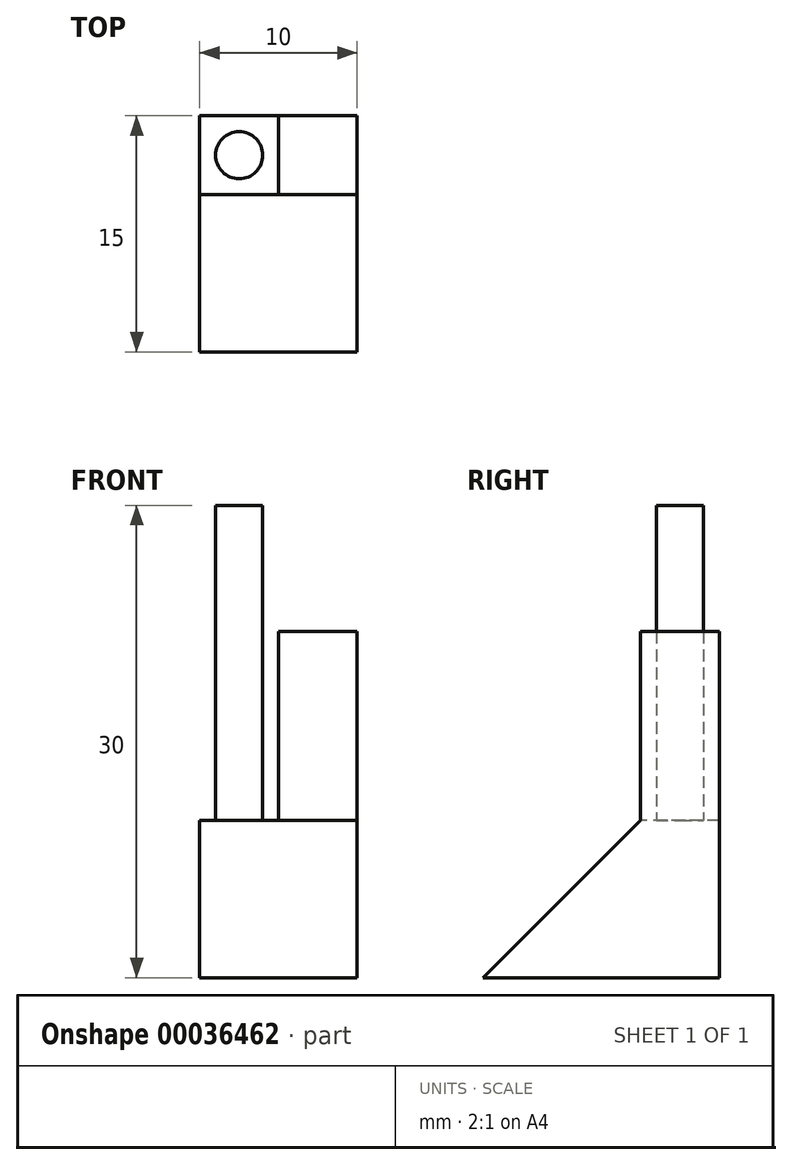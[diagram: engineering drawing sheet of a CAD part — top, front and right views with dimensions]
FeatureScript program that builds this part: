
annotation { "Feature Type Name" : "Feature", "Feature Type Description" : "" }
export const myFeature = defineFeature(function(context is Context, id is Id, definition is map)
    precondition{}
    {
        {
            var Q0;
            Q0=qCreatedBy(makeId("Right.planeOp"),FACE);
            var sketch = newSketch(context, id + "F0", { "sketchPlane" : qUnion([Q0])});
            skLineSegment(sketch, "E0", {"start": v(-10.68, 3.2) * mm, "end": v(-5.68, 3.2) * mm});
            skLineSegment(sketch, "E1", {"start": v(-5.68, 3.2) * mm, "end": v(-5.68, -6.8) * mm});
            skLineSegment(sketch, "E2", {"start": v(-5.68, -6.8) * mm, "end": v(-20.68, -6.8) * mm});
            skLineSegment(sketch, "E3", {"start": v(-20.68, -6.8) * mm, "end": v(-10.68, 3.2) * mm});
            skSolve(sketch);
        }
        {
            var Q0;
            Q0 = qSketchRegion(id + "F0", true);
            extrude(context, id + "F1", {"entities" : qUnion([Q0]), "endBound" : BoundingType.SYMMETRIC, "depth" : 10 * mm});
        }
        {
            var Q0;
            Q0=makeQuery(id+"F1.opExtrude","SWEPT_FACE",FACE,{"disambiguationData":[OSD([sQuery(id+"F0.wireOp",EDGE,"E0")])]});
            var sketch = newSketch(context, id + "F2", { "sketchPlane" : qUnion([Q0])});
            skLineSegment(sketch, "E4.bottom", {"start": v(0, -5.68) * mm, "end": v(5, -5.68) * mm});
            skLineSegment(sketch, "E4.top", {"start": v(0, -10.68) * mm, "end": v(5, -10.68) * mm});
            skLineSegment(sketch, "E4.left", {"start": v(0, -5.68) * mm, "end": v(0, -10.68) * mm});
            skLineSegment(sketch, "E4.right", {"start": v(5, -5.68) * mm, "end": v(5, -10.68) * mm});
            skSolve(sketch);
        }
        {
            var Q0;
            Q0=makeQuery(id+"F2.imprint","IMPRINT",FACE,{"disambiguationData":[TD([[makeQuery(id+"F2.imprint","IMPRINT",EDGE,{"derivedFrom":sQuery(id+"F2.wireOp",EDGE,"E4.bottom")}),1.0]])]});
            extrude(context, id + "F3", {"entities" : qUnion([Q0]), "operationType" : NewBodyOperationType.ADD, "depth" : 12 * mm});
        }
        {
            var Q0;
            Q0=makeQuery(id+"F1.opExtrude","SWEPT_FACE",FACE,{"disambiguationData":[OSD([sQuery(id+"F0.wireOp",EDGE,"E0")])]});
            var sketch = newSketch(context, id + "F4", { "sketchPlane" : qUnion([Q0])});
            skCircle(sketch, "E5", {"center": v(-2.5, -8.18) * mm, "radius": 1.5 * mm});
            skSolve(sketch);
        }
        {
            var Q0;
            Q0=makeQuery(id+"F4.imprint","IMPRINT",FACE,{"disambiguationData":[TD([[makeQuery(id+"F4.imprint","IMPRINT",EDGE,{"derivedFrom":sQuery(id+"F4.wireOp",EDGE,"E5")}),1.0]])]});
            extrude(context, id + "F5", {"entities" : qUnion([Q0]), "operationType" : NewBodyOperationType.ADD, "depth" : 20 * mm});
        }
    });
